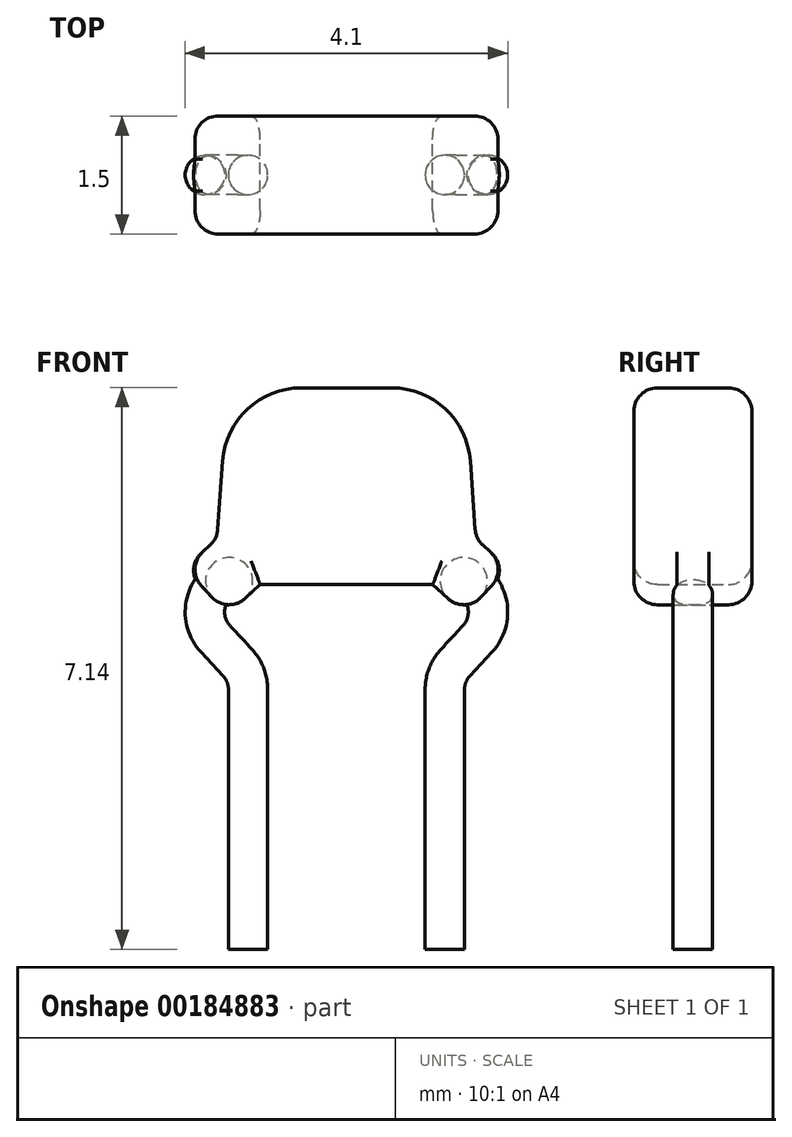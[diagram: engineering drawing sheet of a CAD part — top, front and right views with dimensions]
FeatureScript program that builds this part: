
annotation { "Feature Type Name" : "Feature", "Feature Type Description" : "" }
export const myFeature = defineFeature(function(context is Context, id is Id, definition is map)
    precondition{}
    {
        {
            var Q0;
            Q0=qCreatedBy(makeId("Front.planeOp"),FACE);
            var sketch = newSketch(context, id + "F0", { "sketchPlane" : qUnion([Q0])});
            skLineSegment(sketch, "E0", {"start": v(-1.25, -3.5) * mm, "end": v(-1.25, -0.2) * mm});
            skLineSegment(sketch, "E1", {"start": v(-1.38, 0.14) * mm, "end": v(-1.67, 0.45) * mm});
            skLineSegment(sketch, "E2", {"start": v(-1.63, 1.16) * mm, "end": v(-1.25, 1.5) * mm});
            skPoint(sketch, "E3.visualSharp", {"position": v(-2.01, 0.82) * mm});
            skArc(sketch, "E3.filletArc", {"start": v(-1.63, 1.16) * mm, "mid": v(-1.8, 0.81) * mm, "end": v(-1.67, 0.45) * mm});
            skPoint(sketch, "E4.visualSharp", {"position": v(-1.25, 0) * mm});
            skArc(sketch, "E4.filletArc", {"start": v(-1.25, -0.2) * mm, "mid": v(-1.28, -0.01) * mm, "end": v(-1.38, 0.14) * mm});
            skSolve(sketch);
        }
        {
            var Q0;
            Q0=sQuery(id+"F0.wireOp",EDGE,"E0");
            var Q1;
            Q1=sQuery(id+"F0.wireOp",VERTEX,"E0.start");
            cPlane(context, id + "F1", {"entities" : qUnion([Q0, Q1]), "cplaneType" : CPlaneType.CURVE_POINT, "offset" : 25 * mm, "width" : 150 * mm, "height" : 150 * mm});
        }
        {
            var Q0;
            Q0=qCreatedBy(id+"F1.planeOp",FACE);
            var sketch = newSketch(context, id + "F2", { "sketchPlane" : qUnion([Q0])});
            skCircle(sketch, "E5", {"center": v(-1.25, 0) * mm, "radius": 0.25 * mm});
            skSolve(sketch);
        }
        {
            var Q0;
            Q0=qSketchRegion(id+"F2",true);
            var Q1;
            Q1=qConstructionFilter(qBodyType(qCreatedBy(id+"F0",EDGE),BodyType.WIRE),ConstructionObject.NO);
            sweep(context, id + "F3", {"profiles" : qUnion([Q0]), "path" : qUnion([Q1])});
        }
        {
            var Q0;
            Q0=makeQuery(id+"F3.opSweep","SWEPT_BODY",BODY,{"disambiguationData":[OSD([sQuery(id+"F0.wireOp",EDGE,"E2"),sQuery(id+"F2.wireOp",EDGE,"E5")])]});
            var Q1;
            Q1=qCreatedBy(makeId("Right.planeOp"),FACE);
            mirror(context, id + "F4", {"entities" : qUnion([Q0]), "mirrorPlane" : qUnion([Q1])});
        }
        {
            var Q0;
            Q0=qCreatedBy(makeId("Front.planeOp"),FACE);
            var sketch = newSketch(context, id + "F5", { "sketchPlane" : qUnion([Q0])});
            skLineSegment(sketch, "E6", {"start": v(0, 3.64) * mm, "end": v(-0.57, 3.64) * mm});
            skLineSegment(sketch, "E7", {"start": v(-1.57, 2.7) * mm, "end": v(-1.64, 1.72) * mm});
            skLineSegment(sketch, "E8", {"start": v(-1.64, 1.72) * mm, "end": v(-2.05, 1.35) * mm});
            skLineSegment(sketch, "E9", {"start": v(-2.05, 1.35) * mm, "end": v(-1.5, 0.76) * mm});
            skLineSegment(sketch, "E10", {"start": v(-1.5, 0.76) * mm, "end": v(-1.1, 1.14) * mm});
            skLineSegment(sketch, "E11", {"start": v(-1.1, 1.14) * mm, "end": v(0, 1.14) * mm});
            skLineSegment(sketch, "E12", {"start": v(0, 1.14) * mm, "end": v(0, 3.64) * mm});
            skPoint(sketch, "E13.visualSharp", {"position": v(-1.5, 3.64) * mm});
            skArc(sketch, "E13.filletArc", {"start": v(-0.57, 3.64) * mm, "mid": v(-1.26, 3.37) * mm, "end": v(-1.57, 2.7) * mm});
            skSolve(sketch);
        }
        {
            var Q0;
            Q0=qSketchRegion(id+"F5",true);
            extrude(context, id + "F6", {"entities" : qUnion([Q0]), "operationType" : NewBodyOperationType.ADD, "endBound" : BoundingType.SYMMETRIC, "depth" : 1.5 * mm});
        }
        {
            var Q0;
            Q0=makeQuery(id+"F3.opSweep","SWEPT_BODY",BODY,{"disambiguationData":[OSD([sQuery(id+"F0.wireOp",EDGE,"E2"),sQuery(id+"F2.wireOp",EDGE,"E5")])]});
            var Q1;
            Q1=makeQuery(id+"F6.opExtrude","SWEPT_FACE",FACE,{"disambiguationData":[OSD([sQuery(id+"F5.wireOp",EDGE,"E12")])]});
            mirror(context, id + "F7", {"operationType" : NewBodyOperationType.ADD, "entities" : qUnion([Q0]), "mirrorPlane" : qUnion([Q1])});
        }
        {
            var Q0;
            {var subQ0=makeQuery(id+"F6.opExtrude","CAP_FACE",FACE,{"disambiguationData":[OSD([sQuery(id+"F5.wireOp",EDGE,"E6"),sQuery(id+"F5.wireOp",EDGE,"E7"),sQuery(id+"F5.wireOp",EDGE,"E8"),sQuery(id+"F5.wireOp",EDGE,"E9"),sQuery(id+"F5.wireOp",EDGE,"E10"),sQuery(id+"F5.wireOp",EDGE,"E11"),sQuery(id+"F5.wireOp",EDGE,"E12"),sQuery(id+"F5.wireOp",EDGE,"E13.filletArc")])],"isStart":false});Q0=makeQuery(id+"F7.boolean.opBoolean","MERGE",FACE,{"derivedFrom":[subQ0,makeQuery(id+"F7.opPattern","COPY",FACE,{"derivedFrom":subQ0,"instanceName":"1"})]});}
            var Q1;
            {var subQ0=makeQuery(id+"F6.opExtrude","CAP_FACE",FACE,{"disambiguationData":[OSD([sQuery(id+"F5.wireOp",EDGE,"E6"),sQuery(id+"F5.wireOp",EDGE,"E7"),sQuery(id+"F5.wireOp",EDGE,"E8"),sQuery(id+"F5.wireOp",EDGE,"E9"),sQuery(id+"F5.wireOp",EDGE,"E10"),sQuery(id+"F5.wireOp",EDGE,"E11"),sQuery(id+"F5.wireOp",EDGE,"E12"),sQuery(id+"F5.wireOp",EDGE,"E13.filletArc")])],"isStart":true});Q1=makeQuery(id+"F7.boolean.opBoolean","MERGE",FACE,{"derivedFrom":[subQ0,makeQuery(id+"F7.opPattern","COPY",FACE,{"derivedFrom":subQ0,"instanceName":"1"})]});}
            var Q2;
            Q2=makeQuery(id+"F6.opExtrude","SWEPT_EDGE",EDGE,{"disambiguationData":[OSD([sQuery(id+"F5.wireOp",EDGE,"E8"),sQuery(id+"F5.wireOp",EDGE,"E9")])]});
            var Q3;
            Q3=makeQuery(id+"F6.opExtrude","SWEPT_EDGE",EDGE,{"disambiguationData":[OSD([sQuery(id+"F5.wireOp",EDGE,"E9"),sQuery(id+"F5.wireOp",EDGE,"E10")])]});
            var Q4;
            Q4=makeQuery(id+"F7.opPattern","COPY",EDGE,{"derivedFrom":makeQuery(id+"F6.opExtrude","SWEPT_EDGE",EDGE,{"disambiguationData":[OSD([sQuery(id+"F5.wireOp",EDGE,"E9"),sQuery(id+"F5.wireOp",EDGE,"E10")])]}),"instanceName":"1"});
            var Q5;
            Q5=makeQuery(id+"F7.opPattern","COPY",EDGE,{"derivedFrom":makeQuery(id+"F6.opExtrude","SWEPT_EDGE",EDGE,{"disambiguationData":[OSD([sQuery(id+"F5.wireOp",EDGE,"E8"),sQuery(id+"F5.wireOp",EDGE,"E9")])]}),"instanceName":"1"});
            var Q6;
            Q6=makeQuery(id+"F7.opPattern","COPY",EDGE,{"derivedFrom":makeQuery(id+"F6.opExtrude","SWEPT_EDGE",EDGE,{"disambiguationData":[OSD([sQuery(id+"F5.wireOp",EDGE,"E7"),sQuery(id+"F5.wireOp",EDGE,"E8")])]}),"instanceName":"1"});
            var Q7;
            Q7=makeQuery(id+"F6.opExtrude","SWEPT_EDGE",EDGE,{"disambiguationData":[OSD([sQuery(id+"F5.wireOp",EDGE,"E7"),sQuery(id+"F5.wireOp",EDGE,"E8")])]});
            fillet(context, id + "F8", {"entities" : qUnion([Q0, Q1, Q2, Q3, Q4, Q5, Q6, Q7]), "radius" : 0.3 * mm, "tangentPropagation" : true, "allowEdgeOverflow" : false});
        }
    });
